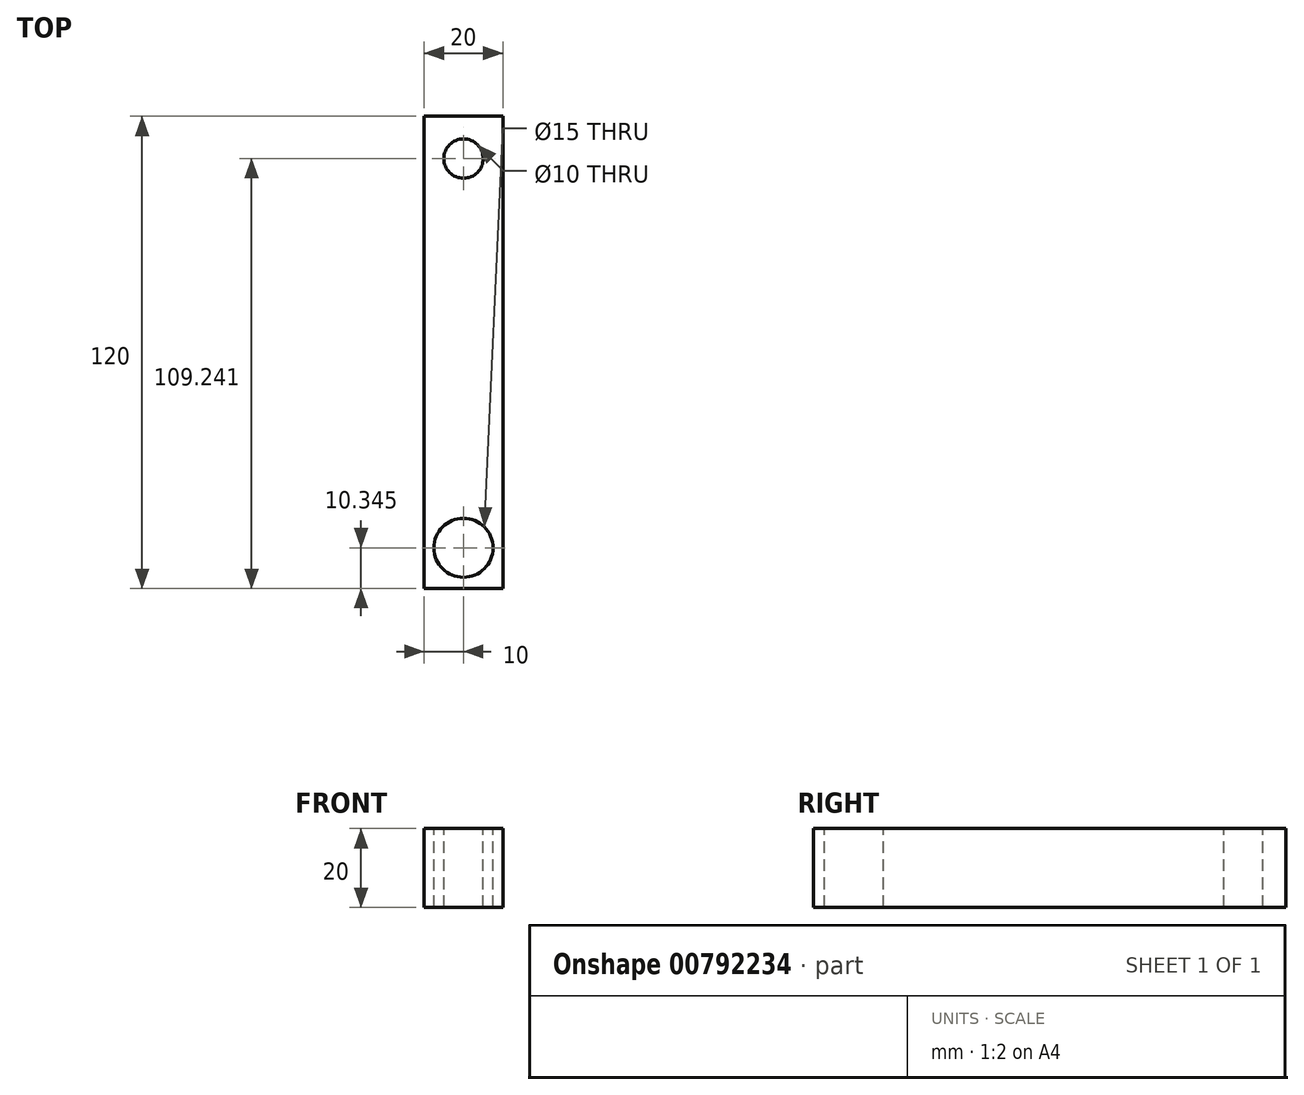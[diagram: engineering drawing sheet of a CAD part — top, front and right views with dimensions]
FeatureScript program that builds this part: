
annotation { "Feature Type Name" : "Feature", "Feature Type Description" : "" }
export const myFeature = defineFeature(function(context is Context, id is Id, definition is map)
    precondition{}
    {
        {
            var Q0;
            Q0=qCreatedBy(makeId("Top.planeOp"),FACE);
            var sketch = newSketch(context, id + "F0", { "sketchPlane" : qUnion([Q0])});
            skLineSegment(sketch, "E0.bottom", {"start": v(10, -60) * mm, "end": v(-10, -60) * mm});
            skLineSegment(sketch, "E0.top", {"start": v(10, 60) * mm, "end": v(-10, 60) * mm});
            skLineSegment(sketch, "E0.left", {"start": v(10, -60) * mm, "end": v(10, 60) * mm});
            skLineSegment(sketch, "E0.right", {"start": v(-10, -60) * mm, "end": v(-10, 60) * mm});
            skPoint(sketch, "E0.middle", {"position": v(0, 0) * mm});
            skSolve(sketch);
        }
        {
            var Q0;
            Q0=makeQuery(id+"F0.imprint","IMPRINT",FACE,{"disambiguationData":[TD([[makeQuery(id+"F0.imprint","IMPRINT",EDGE,{"derivedFrom":sQuery(id+"F0.wireOp",EDGE,"E0.bottom")}),-1.0]])]});
            extrude(context, id + "F1", {"entities" : qUnion([Q0]), "depth" : 20 * mm, "offsetDistance" : 25 * mm});
        }
        {
            var Q0;
            Q0=makeQuery(id+"F1.opExtrude","CAP_FACE",FACE,{"disambiguationData":[OSD([sQuery(id+"F0.wireOp",EDGE,"E0.bottom"),sQuery(id+"F0.wireOp",EDGE,"E0.top"),sQuery(id+"F0.wireOp",EDGE,"E0.left"),sQuery(id+"F0.wireOp",EDGE,"E0.right")])],"isStart":false});
            var sketch = newSketch(context, id + "F2", { "sketchPlane" : qUnion([Q0])});
            skSolve(sketch);
        }
        {
            var Q0;
            Q0=makeQuery(id+"F2.imprint","IMPRINT",FACE,{"disambiguationData":[TD([[makeQuery(id+"F2.imprint","IMPRINT",EDGE,{"derivedFrom":makeQuery(id+"F1.opExtrude","CAP_EDGE",EDGE,{"disambiguationData":[OSD([sQuery(id+"F0.wireOp",EDGE,"E0.bottom")])],"isStart":false})}),-1.0]])]});
            var sketch = newSketch(context, id + "F3", { "sketchPlane" : qUnion([Q0])});
            skCircle(sketch, "E1", {"center": v(0, -49.66) * mm, "radius": 6.1 * mm});
            skSolve(sketch);
        }
        {
            var Q0;
            Q0=sQuery(id+"F3.wireOp",VERTEX,"E1.center");
            var Q1;
            Q1=makeQuery(id+"F1.opExtrude","SWEPT_BODY",BODY,{"disambiguationData":[OSD([sQuery(id+"F0.wireOp",EDGE,"E0.bottom"),sQuery(id+"F0.wireOp",EDGE,"E0.top"),sQuery(id+"F0.wireOp",EDGE,"E0.left"),sQuery(id+"F0.wireOp",EDGE,"E0.right")])]});
            hole(context, id + "F4", {"style" : HoleStyle.SIMPLE, "endStyle" : HoleEndStyle.THROUGH, "holeDiameter" : 15 * mm, "majorDiameter" : 5 * mm, "isTappedThrough" : true, "tappedDepth" : 12 * mm, "tapClearance" : 3, "locations" : qUnion([Q0]), "scope" : qUnion([Q1])});
        }
        {
            var Q0;
            Q0=makeQuery(id+"F2.imprint","IMPRINT",FACE,{"disambiguationData":[TD([[makeQuery(id+"F2.imprint","IMPRINT",EDGE,{"derivedFrom":makeQuery(id+"F1.opExtrude","CAP_EDGE",EDGE,{"disambiguationData":[OSD([sQuery(id+"F0.wireOp",EDGE,"E0.bottom")])],"isStart":false})}),-1.0]])]});
            var sketch = newSketch(context, id + "F5", { "sketchPlane" : qUnion([Q0])});
            skCircle(sketch, "E2", {"center": v(0, 49.24) * mm, "radius": 6.36 * mm});
            skSolve(sketch);
        }
        {
            var Q0;
            Q0=sQuery(id+"F5.wireOp",VERTEX,"E2.center");
            var Q1;
            Q1=makeQuery(id+"F1.opExtrude","SWEPT_BODY",BODY,{"disambiguationData":[OSD([sQuery(id+"F0.wireOp",EDGE,"E0.bottom"),sQuery(id+"F0.wireOp",EDGE,"E0.top"),sQuery(id+"F0.wireOp",EDGE,"E0.left"),sQuery(id+"F0.wireOp",EDGE,"E0.right")])]});
            hole(context, id + "F6", {"style" : HoleStyle.SIMPLE, "endStyle" : HoleEndStyle.THROUGH, "holeDiameter" : 10 * mm, "majorDiameter" : 5 * mm, "isTappedThrough" : true, "tappedDepth" : 12 * mm, "tapClearance" : 3, "locations" : qUnion([Q0]), "scope" : qUnion([Q1])});
        }
    });
